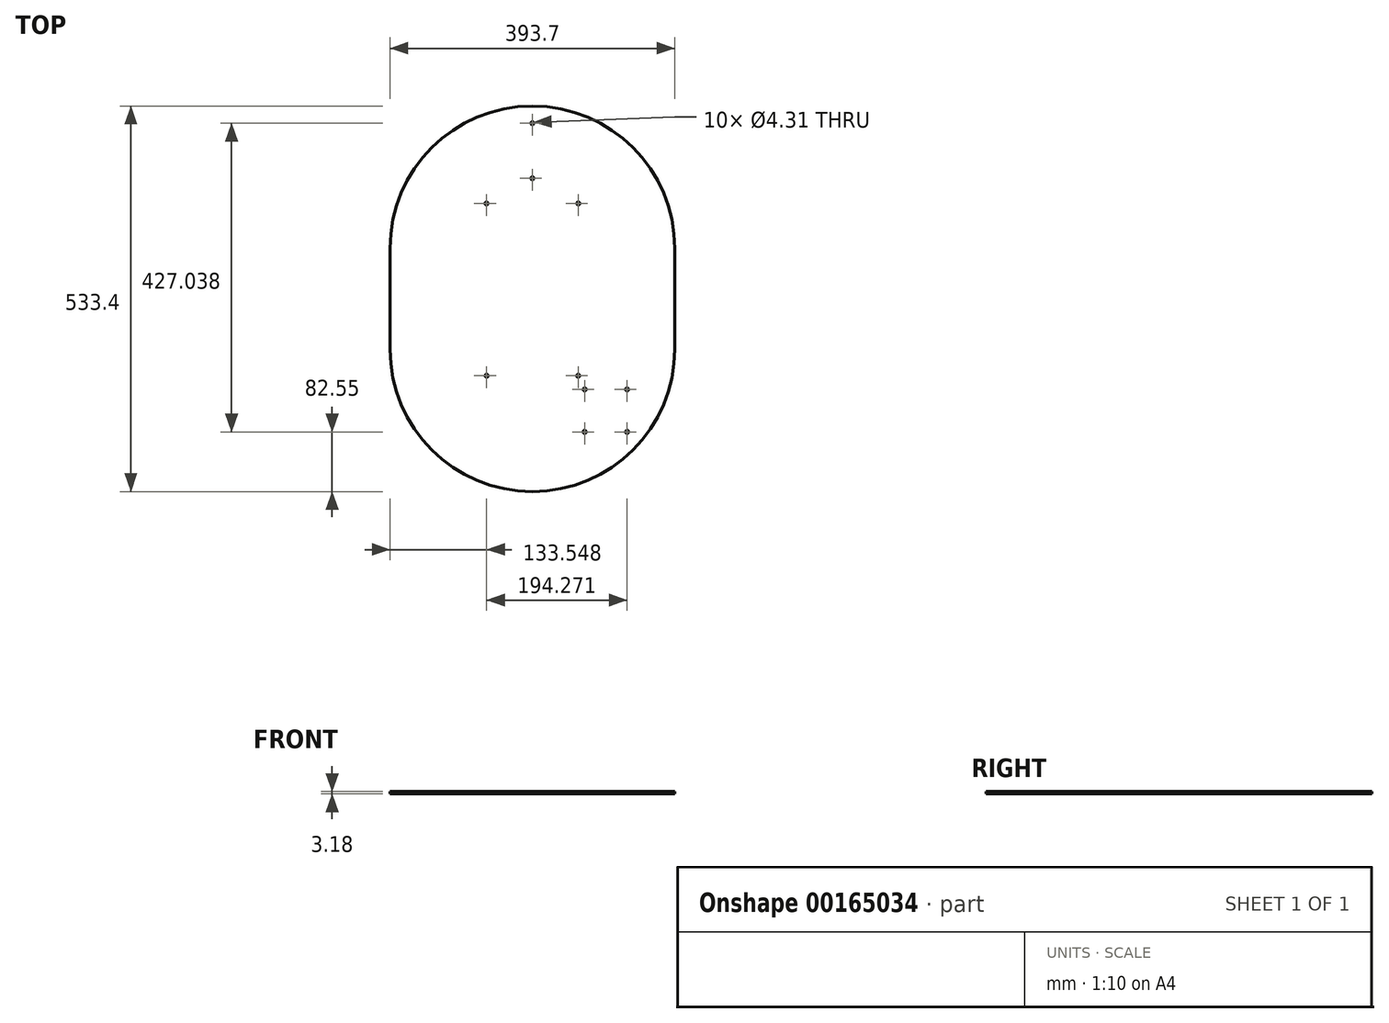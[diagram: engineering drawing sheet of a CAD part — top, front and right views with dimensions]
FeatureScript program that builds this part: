
annotation { "Feature Type Name" : "Feature", "Feature Type Description" : "" }
export const myFeature = defineFeature(function(context is Context, id is Id, definition is map)
    precondition{}
    {
        {
            var Q0;
            Q0=qCreatedBy(makeId("Top.planeOp"),FACE);
            var sketch = newSketch(context, id + "F0", { "sketchPlane" : qUnion([Q0])});
            skLineSegment(sketch, "E0.top", {"start": v(0, -139.7) * mm, "end": v(393.7, -139.7) * mm, "construction": true});
            skLineSegment(sketch, "E0.left", {"start": v(0, 0) * mm, "end": v(0, -139.7) * mm});
            skLineSegment(sketch, "E0.right", {"start": v(393.7, 0) * mm, "end": v(393.7, -139.7) * mm});
            skArc(sketch, "E1", {"start": v(0, -139.7) * mm, "mid": v(196.85, -336.55) * mm, "end": v(393.7, -139.7) * mm});
            skLineSegment(sketch, "E2", {"start": v(196.85, -57.15) * mm, "end": v(196.85, -176.32) * mm, "construction": true});
            skLineSegment(sketch, "E3", {"start": v(196.85, -57.15) * mm, "end": v(196.85, 62.02) * mm, "construction": true});
            skLineSegment(sketch, "E4", {"start": v(133.55, 62.02) * mm, "end": v(260.15, 62.02) * mm, "construction": true});
            skLineSegment(sketch, "E5", {"start": v(260.15, 62.02) * mm, "end": v(196.85, -57.15) * mm, "construction": true});
            skLineSegment(sketch, "E6", {"start": v(196.85, -57.15) * mm, "end": v(133.55, 62.02) * mm, "construction": true});
            skLineSegment(sketch, "E7", {"start": v(133.55, -176.32) * mm, "end": v(260.15, -176.32) * mm, "construction": true});
            skLineSegment(sketch, "E8", {"start": v(196.85, -176.32) * mm, "end": v(196.85, -224.63) * mm, "construction": true});
            skLineSegment(sketch, "E9", {"start": v(196.85, -224.63) * mm, "end": v(298.45, -224.63) * mm, "construction": true});
            skLineSegment(sketch, "E10.bottom", {"start": v(327.82, -195.26) * mm, "end": v(269.08, -195.26) * mm, "construction": true});
            skLineSegment(sketch, "E10.top", {"start": v(327.82, -254) * mm, "end": v(269.08, -254) * mm, "construction": true});
            skLineSegment(sketch, "E10.left", {"start": v(327.82, -195.26) * mm, "end": v(327.82, -254) * mm, "construction": true});
            skLineSegment(sketch, "E10.right", {"start": v(269.08, -195.26) * mm, "end": v(269.08, -254) * mm, "construction": true});
            skPoint(sketch, "E10.middle", {"position": v(298.45, -224.63) * mm});
            skCircle(sketch, "E11", {"center": v(269.08, -195.26) * mm, "radius": 2.15 * mm});
            skCircle(sketch, "E12", {"center": v(269.08, -254) * mm, "radius": 2.15 * mm});
            skCircle(sketch, "E13", {"center": v(327.82, -254) * mm, "radius": 2.15 * mm});
            skCircle(sketch, "E14", {"center": v(327.82, -195.26) * mm, "radius": 2.15 * mm});
            skCircle(sketch, "E15", {"center": v(133.55, -176.32) * mm, "radius": 2.15 * mm});
            skCircle(sketch, "E16", {"center": v(260.15, -176.32) * mm, "radius": 2.15 * mm});
            skCircle(sketch, "E17", {"center": v(260.15, 62.02) * mm, "radius": 2.15 * mm});
            skCircle(sketch, "E18", {"center": v(133.55, 62.02) * mm, "radius": 2.15 * mm});
            skLineSegment(sketch, "E19", {"start": v(0, 0) * mm, "end": v(131.23, 0) * mm, "construction": true});
            skLineSegment(sketch, "E20", {"start": v(131.23, 0) * mm, "end": v(131.23, -57.15) * mm, "construction": true});
            skLineSegment(sketch, "E21", {"start": v(131.23, -57.15) * mm, "end": v(262.47, -57.15) * mm, "construction": true});
            skLineSegment(sketch, "E22", {"start": v(262.47, -57.15) * mm, "end": v(262.47, 0) * mm, "construction": true});
            skLineSegment(sketch, "E23", {"start": v(262.47, 0) * mm, "end": v(393.7, 0) * mm, "construction": true});
            skArc(sketch, "E24", {"start": v(393.7, 0) * mm, "mid": v(196.85, 196.85) * mm, "end": v(0, 0) * mm});
            skLineSegment(sketch, "E25", {"start": v(196.85, 196.85) * mm, "end": v(196.85, 173.04) * mm, "construction": true});
            skLineSegment(sketch, "E26", {"start": v(196.85, 173.04) * mm, "end": v(196.85, 96.84) * mm, "construction": true});
            skCircle(sketch, "E27", {"center": v(196.85, 173.04) * mm, "radius": 2.15 * mm});
            skCircle(sketch, "E28", {"center": v(196.85, 96.84) * mm, "radius": 2.15 * mm});
            skArc(sketch, "E29", {"start": v(260.15, 62.02) * mm, "mid": v(196.85, 77.79) * mm, "end": v(133.55, 62.02) * mm, "construction": true});
            skLineSegment(sketch, "E30", {"start": v(196.85, 96.84) * mm, "end": v(196.85, 77.79) * mm, "construction": true});
            skCircle(sketch, "E31", {"center": v(327.82, -254) * mm, "radius": 23.02 * mm, "construction": true});
            skSolve(sketch);
        }
        {
            var Q0;
            Q0=qSketchRegion(id+"F0",true);
            extrude(context, id + "F1", {"entities" : qUnion([Q0]), "depth" : 3.17 * mm});
        }
    });
